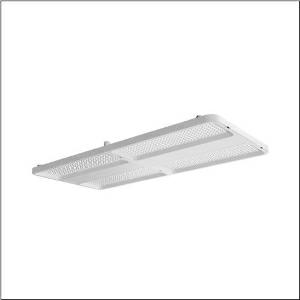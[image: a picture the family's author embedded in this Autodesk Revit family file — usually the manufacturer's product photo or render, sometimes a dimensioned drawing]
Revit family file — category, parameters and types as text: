
# Revit family: highbay_11_maxi_51hn11db3tda
name_source: partatom
category: Lighting Fixtures
units: mm (PartAtom-declared; Revit-internal decimal feet)

## family parameters
Cut with Voids When Loaded = No
Host = Face
Light Source = No
Part Type = Normal
Room Calculation Point = No
Round Connector Dimension = Use Diameter
Shared = No

## types (1)
- --- (1 x LED, 8610 lm, 44.5 W, 3000K)
    Apparent Load = 45 VA
    CIE Flux Codes = 85 97 100 100 100
    Color Rendering = 80
    Color Temperature = 3000K
    Default Elevation = 1800 mm
    Description = high bay luminaire Highbay 11 maxi; direct symmetric narrow distribution, light control with lens of PMMA; UGR ≤ 22 (X = 4H | Y = 8H | S = 0.25H | reflection values 70/50/20); luminous flux: 53.070lm; light colour: 830, colour temperature: 3000K, MacAdam ≤ 2 SDCM (initial), colour rendering: CRI > 80; luminous efficacy: 179,8lm/W; rated service life: 100.000h (L95/B50) at AT= 25°C; control: DALI 2; luminaire connection: terminal, 5-pole, max. 2.5mm² (cable entry for one cable, Ø 8.5..16mm); mains connection: 230..240V, AC/DC 0/50..60Hz; connected load: 295,1W; protection rating (complete): IP66; insulation class (complete): insulation class I (protective earthing); protection symbol: D; impact resistance: IK08; certification: CE, ENEC, VDE, UKCA; luminaire for central battery installations according to DIN EN 60598-2-22, internal wiring halogen-free; luminaire LABS conformity tested according to VDMA 24364:2018-05; corresponds to IFS (International Featured Standards) requirements for safety and quality in the food industry; housing frame of high-performance plastic PA6, matt traffic white (RAL 9016); cover of PMMA; dimension (LxWxH): 946 x 442 x 72mm; permissible operating ambient temperature: -40..+50°C (reducing of maximum allowable ambient temperature of 5°C with ceiling mounting); packaging unit: 1 piece; (delivery without accessories; please order mounting accessories separately)
    Height = 72 mm  [stored 0.23622 ft]
    Lamp = 1 x LED
    Lamp Light Flux = 8610 lm
    Lamp Power = 44.5 W
    Lamp count = 1
    Length = 946 mm
    Luminous efficacy = 193 lm/W
    Manufacturer = Siteco
    ModVariant = No
    Model = 51HN11DB3TDA
    Mounting Place = Ceiling
    Mounting Type = Pendant
    Number of Poles = 1
    OnlyDefault = Yes
    Power Factor = 1
    Product Name = Highbay 11 maxi
    Product group = high bay luminaire
    ProductGroupID = 901
    Protection Class = Protection class I
    Protection Degree = IP 66
    RLX_Detail_Level = 1
    RLX_Emergency_Light_Flux = 0 lm
    RLX_Emergency_Type = 0
    RLX_Emergency_Type_DB = No
    RlxData = <blob elided: 127533 chars, md5=621688d6>
    Socket = socket
    Standby Power = 0 W
    System Light Flux = 8610 lm
    System Power = 45 W
    Type Comments = : DC mode (central or group accumulator) initial emergency light level
    Type Image = l_1363244.jpg
    URL = http://relux.com
    VarID = @adj_000001
    Voltage = 0 V
    Weight = 0.00 kg
    Width = 442 mm

note: [stored X ft] marks values corroborated as IEEE doubles in the binary element streams (Revit-internal decimal feet)

## geometry (parser evidence)
native form markers: Blend x4, Sweep x10
no freeform markers — native parametric forms only
